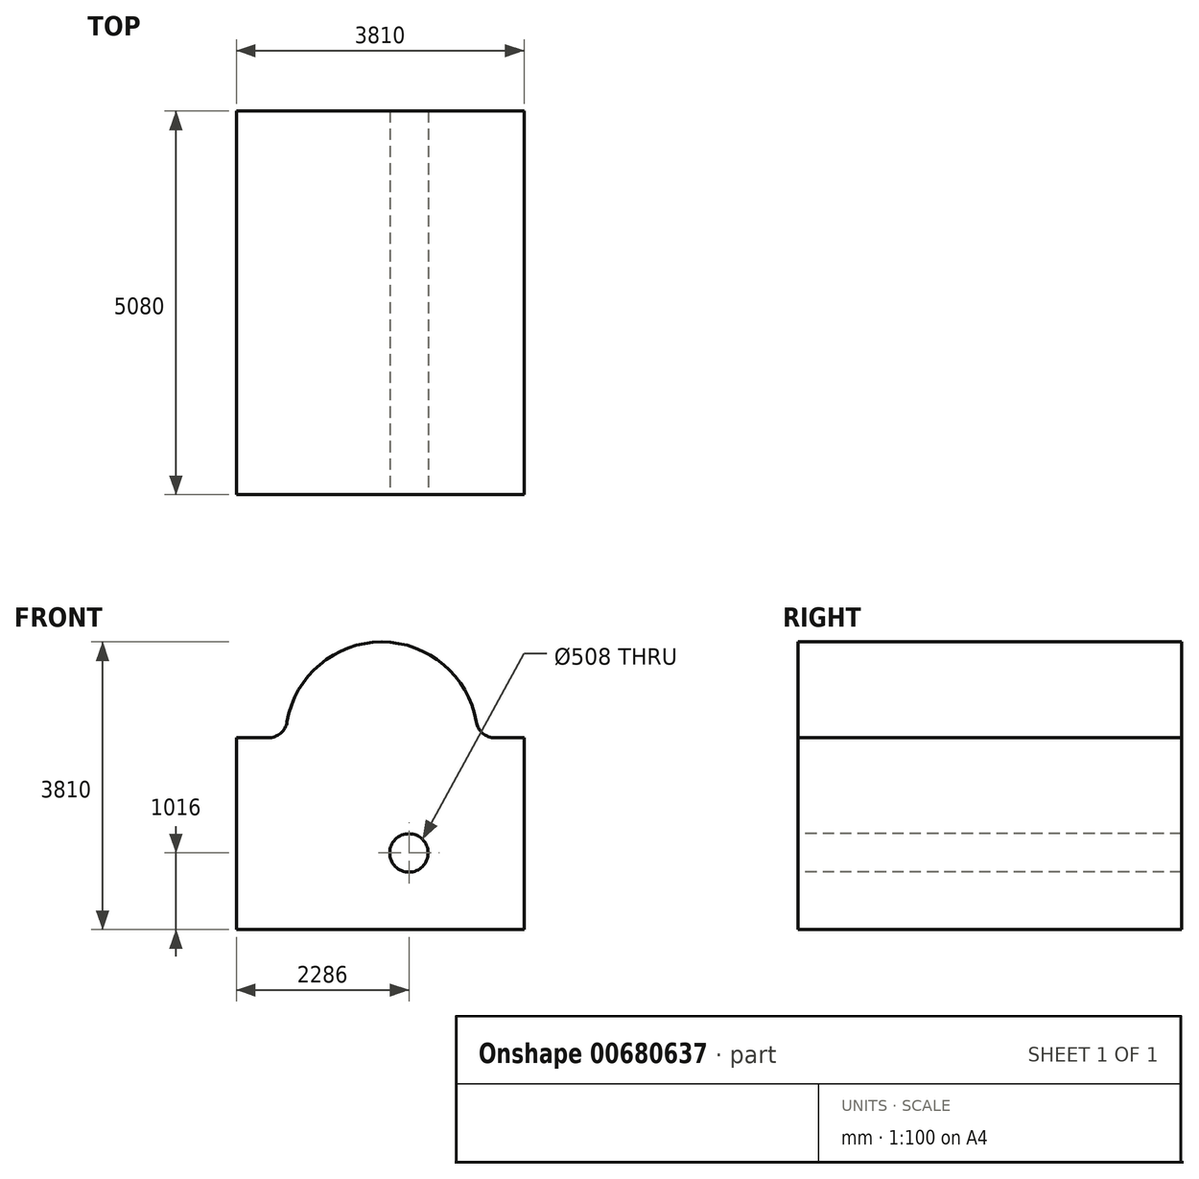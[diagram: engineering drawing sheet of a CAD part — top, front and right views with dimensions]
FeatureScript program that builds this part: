
annotation { "Feature Type Name" : "Feature", "Feature Type Description" : "" }
export const myFeature = defineFeature(function(context is Context, id is Id, definition is map)
    precondition{}
    {
        {
            var Q0;
            Q0=qCreatedBy(makeId("Front.planeOp"),FACE);
            var sketch = newSketch(context, id + "F0", { "sketchPlane" : qUnion([Q0])});
            skLineSegment(sketch, "E0.bottom", {"start": v(-3775.38, 2511.32) * mm, "end": v(-3354.25, 2511.32) * mm});
            skLineSegment(sketch, "E0.top", {"start": v(-3775.38, -28.68) * mm, "end": v(34.62, -28.68) * mm});
            skLineSegment(sketch, "E0.left", {"start": v(-3775.38, 2511.32) * mm, "end": v(-3775.38, -28.68) * mm});
            skLineSegment(sketch, "E0.right", {"start": v(34.62, 2511.32) * mm, "end": v(34.62, -28.68) * mm});
            skArc(sketch, "E1", {"start": v(-3103.8, 2722.99) * mm, "mid": v(-1851.57, 3781.32) * mm, "end": v(-599.33, 2722.99) * mm});
            skPoint(sketch, "E2.newPointB", {"position": v(72.25, 2511.32) * mm});
            skArc(sketch, "E3.filletArc", {"start": v(-3354.25, 2511.32) * mm, "mid": v(-3190.3, 2571.32) * mm, "end": v(-3103.8, 2722.99) * mm});
            skLineSegment(sketch, "E4", {"start": v(34.62, 2511.32) * mm, "end": v(-348.88, 2511.32) * mm});
            skPoint(sketch, "E5.visualSharp", {"position": v(-581.57, 2511.32) * mm});
            skArc(sketch, "E5.filletArc", {"start": v(-599.33, 2722.99) * mm, "mid": v(-512.84, 2571.32) * mm, "end": v(-348.88, 2511.32) * mm});
            skSolve(sketch);
        }
        {
            var Q0;
            Q0=makeQuery(id+"F0.imprint","IMPRINT",FACE,{"disambiguationData":[TD([[makeQuery(id+"F0.imprint","IMPRINT",EDGE,{"derivedFrom":sQuery(id+"F0.wireOp",EDGE,"E0.bottom")}),-1.0]])]});
            extrude(context, id + "F1", {"entities" : qUnion([Q0]), "oppositeDirection" : true, "depth" : 5080 * mm, "offsetDistance" : 25.4 * mm});
        }
        {
            var Q0;
            Q0=makeQuery(id+"F1.opExtrude","CAP_FACE",FACE,{"disambiguationData":[OSD([sQuery(id+"F0.wireOp",EDGE,"E0.bottom"),sQuery(id+"F0.wireOp",EDGE,"E0.top"),sQuery(id+"F0.wireOp",EDGE,"E0.left"),sQuery(id+"F0.wireOp",EDGE,"E0.right"),sQuery(id+"F0.wireOp",EDGE,"E1"),sQuery(id+"F0.wireOp",EDGE,"E3.filletArc"),sQuery(id+"F0.wireOp",EDGE,"E4"),sQuery(id+"F0.wireOp",EDGE,"E5.filletArc")])],"isStart":true});
            var sketch = newSketch(context, id + "F2", { "sketchPlane" : qUnion([Q0])});
            skCircle(sketch, "E6", {"center": v(-1489.38, 987.32) * mm, "radius": 254 * mm});
            skSolve(sketch);
        }
        {
            var Q0;
            Q0=makeQuery(id+"F2.imprint","IMPRINT",FACE,{"disambiguationData":[TD([[makeQuery(id+"F2.imprint","IMPRINT",EDGE,{"derivedFrom":sQuery(id+"F2.wireOp",EDGE,"E6")}),-1.0]])]});
            var Q1;
            Q1=sQuery(id+"F2.wireOp",EDGE,"E6");
            extrude(context, id + "F3", {"entities" : qUnion([Q0]), "operationType" : NewBodyOperationType.INTERSECT, "surfaceEntities" : qUnion([Q1]), "oppositeDirection" : true, "depth" : 7620 * mm, "offsetDistance" : 25.4 * mm});
        }
    });
